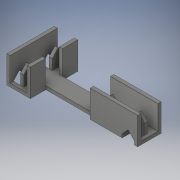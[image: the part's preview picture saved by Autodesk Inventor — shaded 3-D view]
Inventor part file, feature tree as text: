
AUTODESK INVENTOR PART (.ipt)
format: ipt  version: 2019 (Build 230136000, 136)  size: 677,376 bytes
history: native  units: mm
features: sketch x9, extrude x8, projected_geometry x2, plane x1, mirror x1, other x1, pattern_circular x1, fillet x1
ambient origin geometry x8: Origin, YZ Plane, XZ Plane, XY Plane, X Axis, Y Axis, Z Axis, Center Point
bodies: Solid1 (feature_tree)
feature tree (24):
  extrude  "Extrusion1"  Depth=10.0mm
  extrude  "Extrusion2"  Depth=10.0mm
  extrude  "Extrusion7"  Depth=10.0mm
  extrude  "Extrusion8"  Depth=0.75mm
  extrude  "Extrusion9"  Depth=0.75mm
  extrude  "Extrusion10"  Depth=0.75mm
  plane  "Work Plane1"
  mirror  "Mirror1"
  extrude  "Extrusion11"  Depth=20.75mm
  extrude  "Extrusion12"  Depth=0.75mm
  sketch  "Sketch12"  dims[d22=5.0mm d23=0.0mm d55=0.75mm d56=0.75mm d57=2.5mm d58=2.5mm d59=0.75mm d60=0.75mm d61=1.375mm d62=1.375mm d63=3.5mm d64=0.0mm d65=2.5mm d66=6.0mm d67=0.75mm d68=0.0mm d69=2.5mm d70=0.75mm d71=2.125mm d72=0.75mm d73=90.0deg d74=0.75mm d75=90.0deg d76=0.75mm d77=0.0mm d78=1.375mm d79=0.75mm d80=0.0mm d81=2.5mm d82=0.75mm d83=0.75mm d84=0.75mm d85=2.125mm d86=2.125mm d87=0.0mm d88=2.125mm d89=2.5mm d90=1.375mm d91=0.75mm d92=0.0mm d93=5.0mm d94=1.75mm d95=20.0mm d96=360.0deg d98=0.05mm d99=0.05mm d100=0.05mm]
  other  "Work Axis2"
  pattern_circular  "Circular Pattern2"  [2 undecoded]
  fillet  "Fillet1"  Radius=0.75mm
  sketch  "Sketch1"  dims[d0=5.0mm d1=10.0mm]
  sketch  "Sketch2"  dims[d2=10.0mm d3=5.0mm]
  sketch  "Sketch6"  dims[d4=10.0mm d5=3.25mm]
  sketch  "Sketch7"  dims[d6=3.25mm d7=0.75mm]
  projected_geometry  "Projected Loop2"
  sketch  "Sketch8"  dims[d13=0.75mm d14=0.0mm d15=0.75mm]
  sketch  "Sketch9"  dims[d16=0.75mm d17=0.75mm]
  projected_geometry  "Projected Loop3"
  sketch  "Sketch10"  dims[d18=20.0mm d19=20.75mm]
  sketch  "Sketch11"  dims[d20=4.25mm d21=0.75mm]
note: 2 required parameter values undecoded (feature->parameter linkage not recoverable at this tier; creation-order binding heuristic only, values carry confidence <= 0.55)
